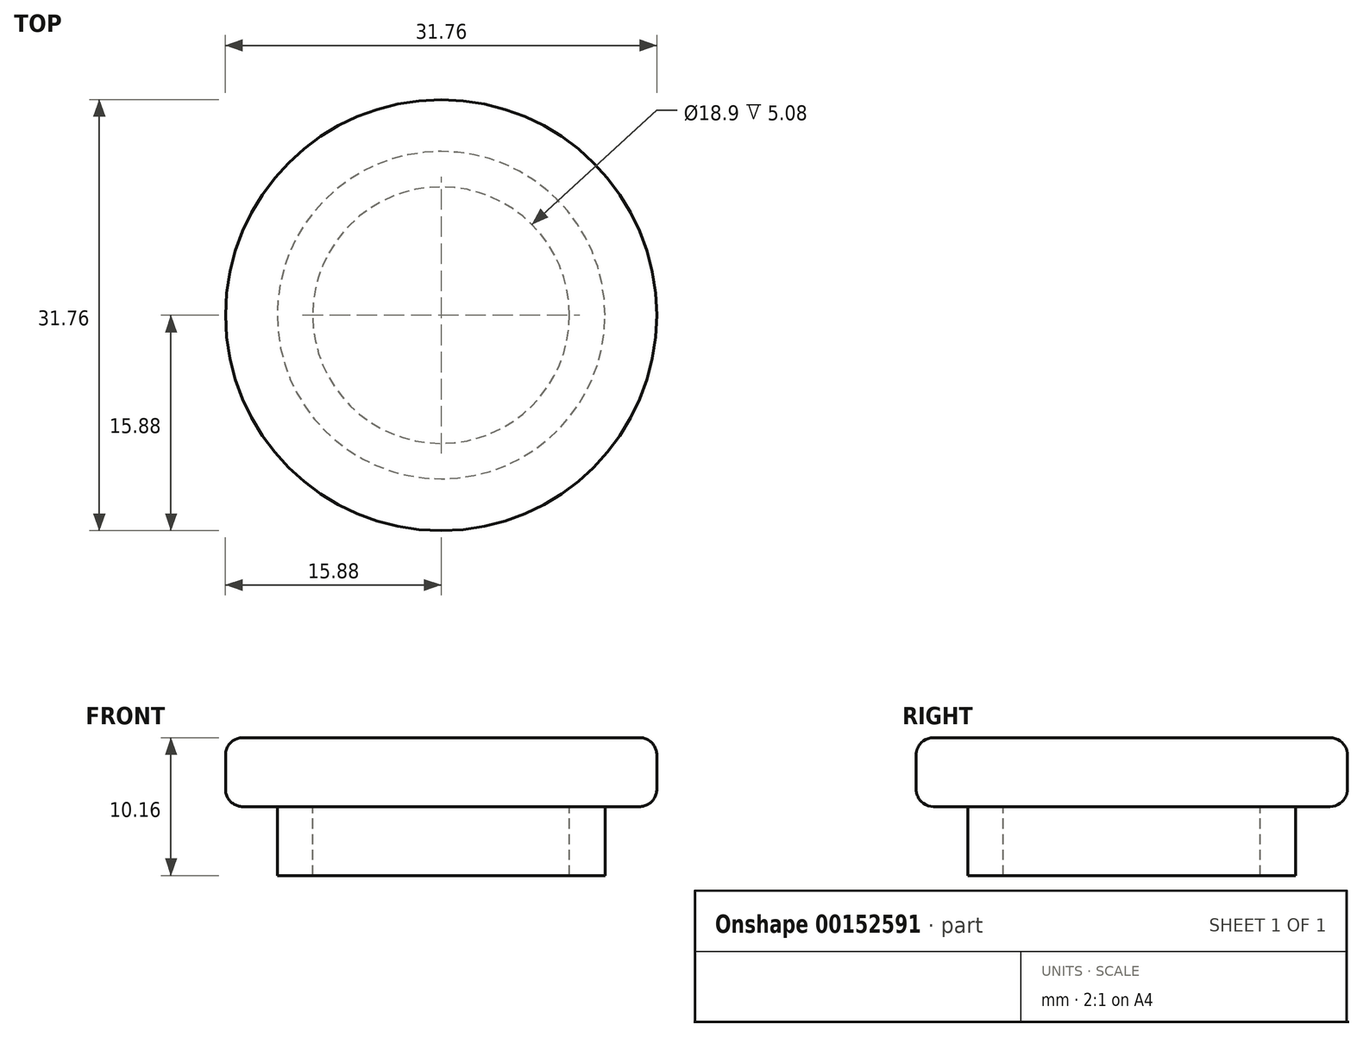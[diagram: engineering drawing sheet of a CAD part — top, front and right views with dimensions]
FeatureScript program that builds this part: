
annotation { "Feature Type Name" : "Feature", "Feature Type Description" : "" }
export const myFeature = defineFeature(function(context is Context, id is Id, definition is map)
    precondition{}
    {
        {
            var Q0;
            Q0=qCreatedBy(makeId("Top.planeOp"),FACE);
            var sketch = newSketch(context, id + "F0", { "sketchPlane" : qUnion([Q0])});
            skCircle(sketch, "E0", {"center": v(0, 0) * mm, "radius": 15.88 * mm});
            skCircle(sketch, "E1", {"center": v(0, 0) * mm, "radius": 12.07 * mm});
            skCircle(sketch, "E2", {"center": v(0, 0) * mm, "radius": 9.45 * mm});
            skSolve(sketch);
        }
        {
            var Q0;
            Q0=makeQuery(id+"F0.imprint","IMPRINT",FACE,{"disambiguationData":[TD([[makeQuery(id+"F0.imprint","IMPRINT",EDGE,{"derivedFrom":sQuery(id+"F0.wireOp",EDGE,"E0")}),1.0]])]});
            var Q1;
            Q1=makeQuery(id+"F0.imprint","IMPRINT",FACE,{"disambiguationData":[TD([[makeQuery(id+"F0.imprint","IMPRINT",EDGE,{"derivedFrom":sQuery(id+"F0.wireOp",EDGE,"E1")}),1.0]])]});
            var Q2;
            Q2=makeQuery(id+"F0.imprint","IMPRINT",FACE,{"disambiguationData":[TD([[makeQuery(id+"F0.imprint","IMPRINT",EDGE,{"derivedFrom":sQuery(id+"F0.wireOp",EDGE,"E2")}),1.0]])]});
            extrude(context, id + "F1", {"entities" : qUnion([Q0, Q1, Q2]), "depth" : 5.08 * mm});
        }
        {
            var Q0;
            Q0=makeQuery(id+"F0.imprint","IMPRINT",FACE,{"disambiguationData":[TD([[makeQuery(id+"F0.imprint","IMPRINT",EDGE,{"derivedFrom":sQuery(id+"F0.wireOp",EDGE,"E1")}),1.0]])]});
            extrude(context, id + "F2", {"entities" : qUnion([Q0]), "operationType" : NewBodyOperationType.ADD, "oppositeDirection" : true, "depth" : 5.08 * mm});
        }
        {
            var Q0;
            Q0=makeQuery(id+"F1.opExtrude","CAP_EDGE",EDGE,{"disambiguationData":[OSD([sQuery(id+"F0.wireOp",EDGE,"E0")])],"isStart":false});
            var Q1;
            Q1=makeQuery(id+"F1.opExtrude","CAP_EDGE",EDGE,{"disambiguationData":[OSD([sQuery(id+"F0.wireOp",EDGE,"E0")])],"isStart":true});
            fillet(context, id + "F3", {"entities" : qUnion([Q0, Q1]), "radius" : 1.27 * mm, "tangentPropagation" : true, "allowEdgeOverflow" : false});
        }
    });
